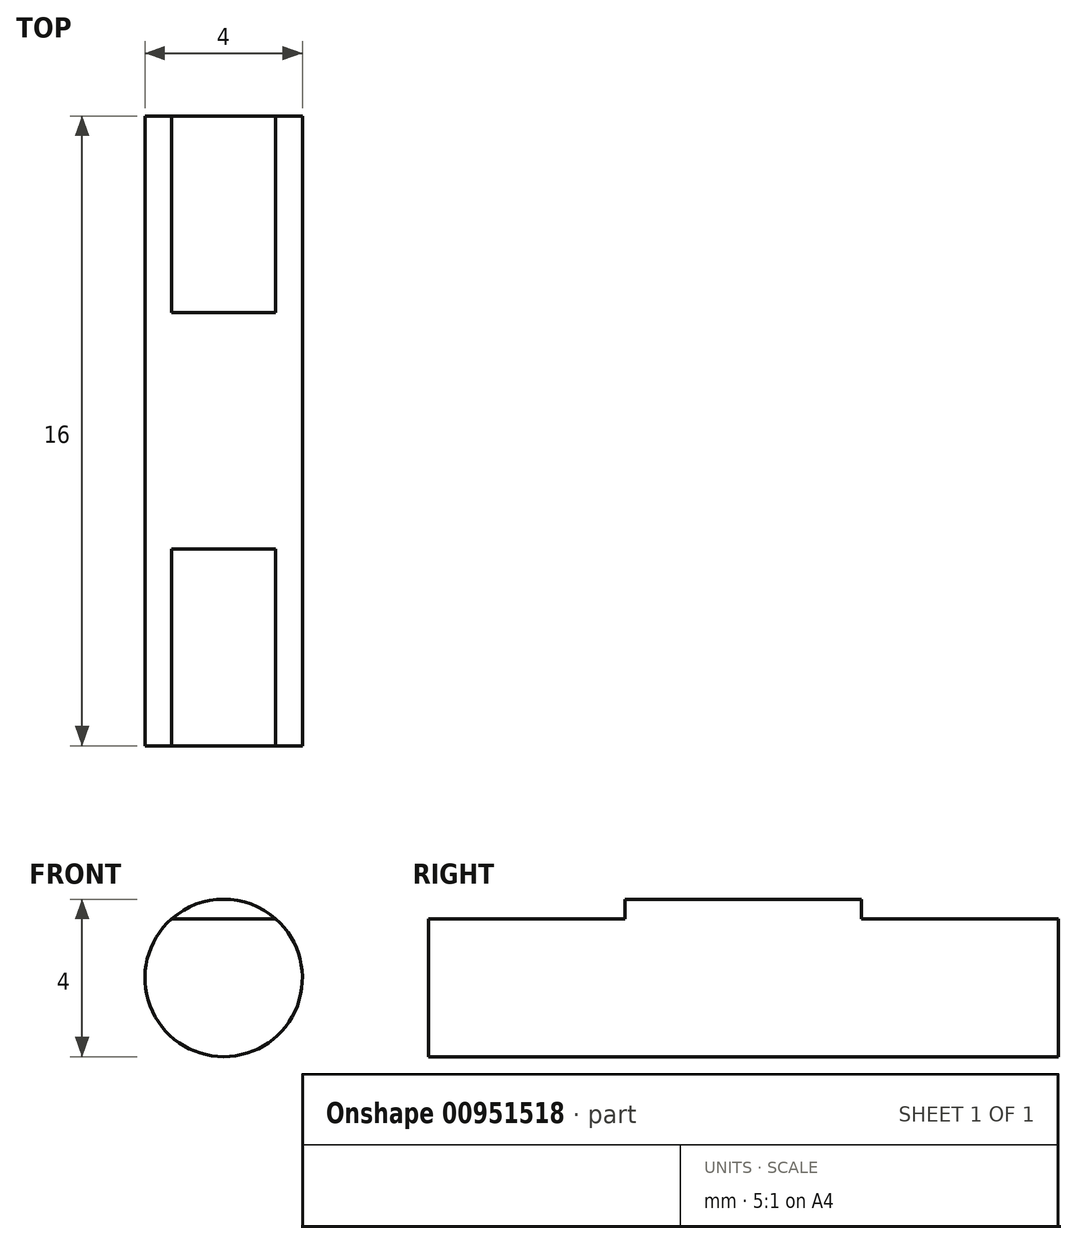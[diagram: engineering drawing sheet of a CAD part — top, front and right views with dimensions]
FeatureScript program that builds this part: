
annotation { "Feature Type Name" : "Feature", "Feature Type Description" : "" }
export const myFeature = defineFeature(function(context is Context, id is Id, definition is map)
    precondition{}
    {
        {
            var Q0;
            Q0=qCreatedBy(makeId("Front.planeOp"),FACE);
            var sketch = newSketch(context, id + "F0", { "sketchPlane" : qUnion([Q0])});
            skCircle(sketch, "E0", {"center": v(0, 0) * mm, "radius": 2 * mm});
            skLineSegment(sketch, "E1", {"start": v(-1.32, 1.5) * mm, "end": v(1.32, 1.5) * mm});
            skSolve(sketch);
        }
        {
            var Q0;
            {var subQ0=sQuery(id+"F0.wireOp",EDGE,"E1");Q0=makeQuery(id+"F0.imprint","IMPRINT",FACE,{"disambiguationData":[TD([[makeQuery(id+"F0.imprint","IMPRINT",EDGE,{"derivedFrom":subQ0}),-1.0]])]});}
            extrude(context, id + "F1", {"entities" : qUnion([Q0]), "depth" : 16 * mm, "offsetDistance" : 25 * mm});
        }
        {
            var Q0;
            Q0=makeQuery(id+"F1.opExtrude","CAP_FACE",FACE,{"disambiguationData":[OSD([sQuery(id+"F0.wireOp",EDGE,"E0"),sQuery(id+"F0.wireOp",EDGE,"E1")])],"isStart":false});
            var sketch = newSketch(context, id + "F2", { "sketchPlane" : qUnion([Q0])});
            skCircle(sketch, "E2", {"center": v(0, 0) * mm, "radius": 2 * mm});
            skSolve(sketch);
        }
        {
            var Q0;
            Q0 = qSketchRegion(id + "F2", true);
            extrude(context, id + "F3", {"entities" : qUnion([Q0]), "operationType" : NewBodyOperationType.ADD, "oppositeDirection" : true, "depth" : 11 * mm, "offsetDistance" : 25 * mm, "hasSecondDirection" : true, "secondDirectionOppositeDirection" : true, "secondDirectionDepth" : 5 * mm});
        }
    });
